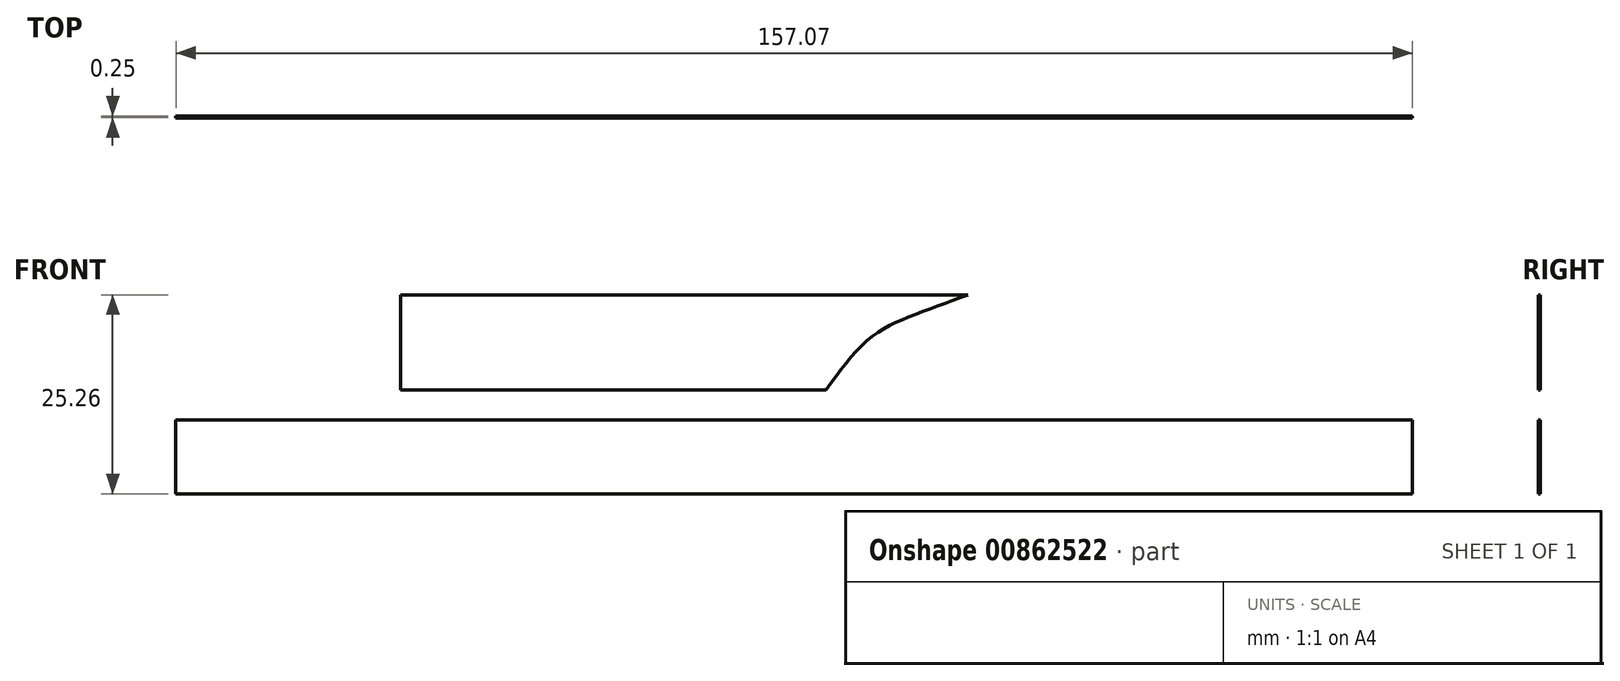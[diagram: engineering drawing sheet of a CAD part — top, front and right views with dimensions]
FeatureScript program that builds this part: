
annotation { "Feature Type Name" : "Feature", "Feature Type Description" : "" }
export const myFeature = defineFeature(function(context is Context, id is Id, definition is map)
    precondition{}
    {
        {
            var Q0;
            Q0=qCreatedBy(makeId("Front.planeOp"),FACE);
            var sketch = newSketch(context, id + "F0", { "sketchPlane" : qUnion([Q0])});
            skLineSegment(sketch, "E0.bottom", {"start": v(-38.44, 12.08) * mm, "end": v(15.58, 12.08) * mm});
            skLineSegment(sketch, "E0.top", {"start": v(-38.44, 0) * mm, "end": v(15.58, 0) * mm});
            skLineSegment(sketch, "E0.left", {"start": v(-38.44, 12.08) * mm, "end": v(-38.44, 0) * mm});
            skLineSegment(sketch, "E0.right", {"start": v(15.58, 12.08) * mm, "end": v(15.58, 0) * mm});
            skLineSegment(sketch, "E1.bottom", {"start": v(-67.01, -3.78) * mm, "end": v(90.06, -3.78) * mm});
            skLineSegment(sketch, "E1.top", {"start": v(-67.01, -13.18) * mm, "end": v(90.06, -13.18) * mm});
            skLineSegment(sketch, "E1.left", {"start": v(-67.01, -3.78) * mm, "end": v(-67.01, -13.18) * mm});
            skLineSegment(sketch, "E1.right", {"start": v(90.06, -3.78) * mm, "end": v(90.06, -13.18) * mm});
            skLineSegment(sketch, "E2", {"start": v(15.58, 12.08) * mm, "end": v(33.63, 12.08) * mm});
            skFitSpline(sketch, "E3", {"points": [v(33.63, 12.08) * mm, v(26.05, 9.25) * mm, v(20.76, 6.26) * mm, v(15.58, 0) * mm], "startDerivative": vector(-22.77, -8.11) * mm, "endDerivative": vector(-14.37, -20.05) * mm});
            skSolve(sketch);
        }
        {
            var Q0;
            Q0=makeQuery(id+"F0.imprint","IMPRINT",FACE,{"disambiguationData":[TD([[makeQuery(id+"F0.imprint","IMPRINT",EDGE,{"derivedFrom":sQuery(id+"F0.wireOp",EDGE,"E0.bottom")}),-1.0]])]});
            var Q1;
            Q1=makeQuery(id+"F0.imprint","IMPRINT",FACE,{"disambiguationData":[TD([[makeQuery(id+"F0.imprint","IMPRINT",EDGE,{"derivedFrom":sQuery(id+"F0.wireOp",EDGE,"E1.bottom")}),-1.0]])]});
            var Q2;
            Q2=makeQuery(id+"F0.imprint","IMPRINT",FACE,{"disambiguationData":[TD([[makeQuery(id+"F0.imprint","IMPRINT",EDGE,{"derivedFrom":sQuery(id+"F0.wireOp",EDGE,"E0.right")}),1.0]])]});
            extrude(context, id + "F1", {"entities" : qUnion([Q0, Q1, Q2]), "depth" : 0.25 * mm, "offsetDistance" : 25.4 * mm});
        }
    });
